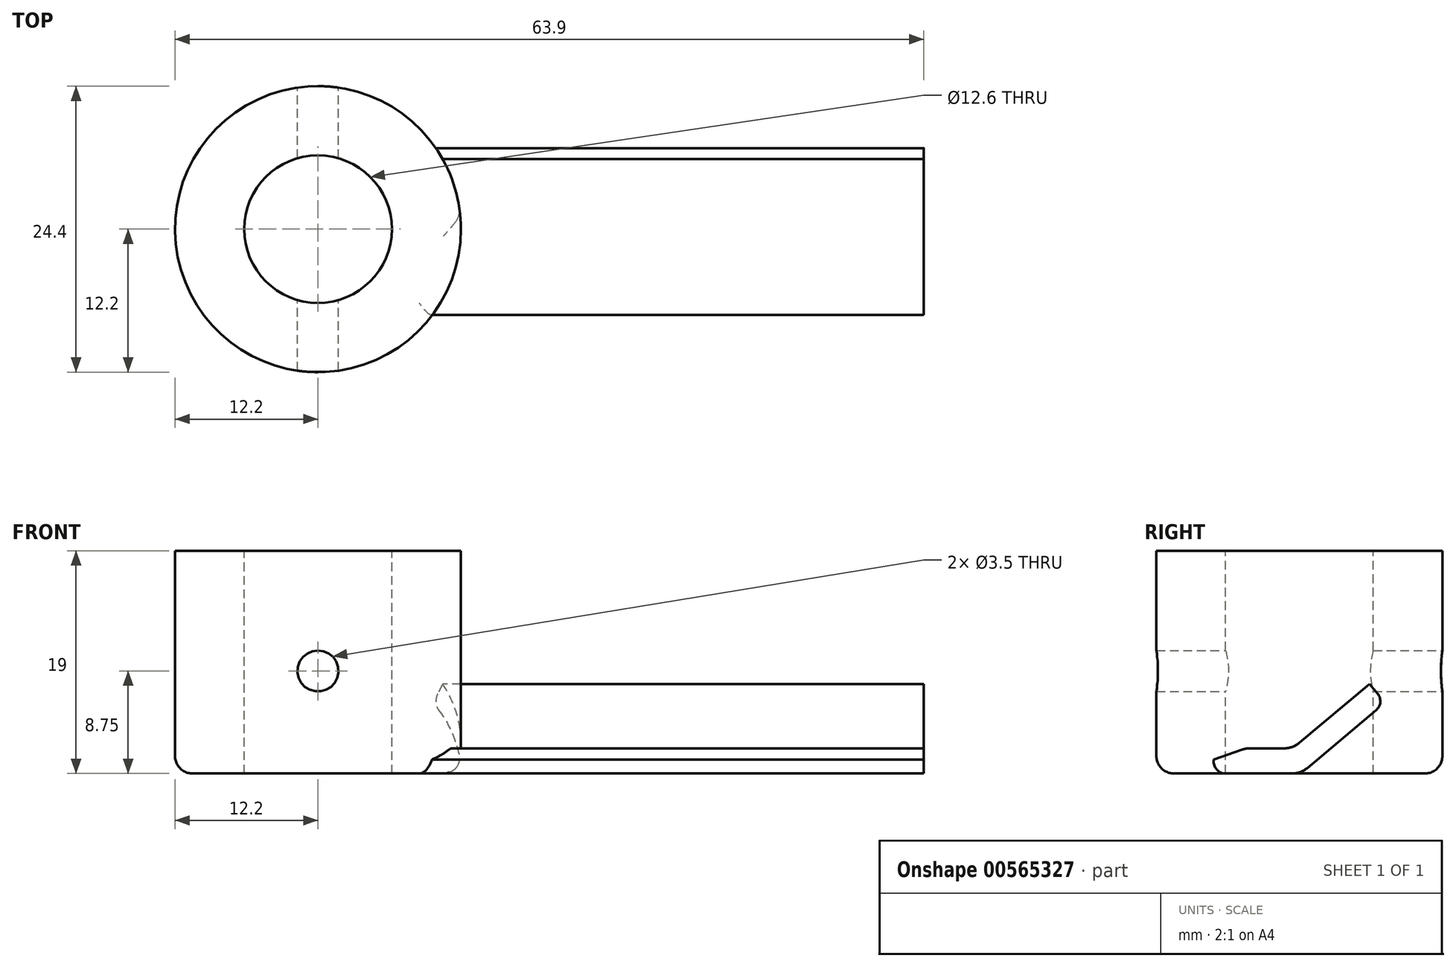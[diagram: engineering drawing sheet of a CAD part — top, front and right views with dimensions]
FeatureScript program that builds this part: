
annotation { "Feature Type Name" : "Feature", "Feature Type Description" : "" }
export const myFeature = defineFeature(function(context is Context, id is Id, definition is map)
    precondition{}
    {
        {
            var Q0;
            Q0=qCreatedBy(makeId("Top.planeOp"),FACE);
            var sketch = newSketch(context, id + "F0", { "sketchPlane" : qUnion([Q0])});
            skCircle(sketch, "E0", {"center": v(0, 0) * mm, "radius": 12.2 * mm});
            skSolve(sketch);
        }
        {
            var Q0;
            Q0 = qSketchRegion(id + "F0", true);
            extrude(context, id + "F1", {"entities" : qUnion([Q0]), "depth" : 19 * mm, "offsetDistance" : 25 * mm});
        }
        {
            var Q0;
            Q0=qCreatedBy(makeId("Right.planeOp"),FACE);
            var sketch = newSketch(context, id + "F2", { "sketchPlane" : qUnion([Q0])});
            skLineSegment(sketch, "E1", {"start": v(-7.31, 0) * mm, "end": v(-7.31, 1.2) * mm});
            skLineSegment(sketch, "E2", {"start": v(-7.31, 1.2) * mm, "end": v(-4.56, 2.15) * mm});
            skLineSegment(sketch, "E3", {"start": v(-4.56, 2.15) * mm, "end": v(-0.56, 2.15) * mm});
            skLineSegment(sketch, "E4", {"start": v(-0.56, 2.15) * mm, "end": v(5.97, 7.64) * mm});
            skLineSegment(sketch, "E5", {"start": v(5.97, 7.64) * mm, "end": v(7.31, 6.05) * mm});
            skLineSegment(sketch, "E6", {"start": v(7.31, 6.05) * mm, "end": v(0.11, 0) * mm});
            skLineSegment(sketch, "E7", {"start": v(0.11, 0) * mm, "end": v(-7.31, 0) * mm});
            skSolve(sketch);
        }
        {
            var Q0;
            Q0 = qSketchRegion(id + "F2", true);
            extrude(context, id + "F3", {"entities" : qUnion([Q0]), "operationType" : NewBodyOperationType.ADD, "depth" : 51.7 * mm, "offsetDistance" : 25 * mm});
        }
        {
            var Q0;
            Q0=makeQuery(id+"F1.opExtrude","CAP_FACE",FACE,{"disambiguationData":[OSD([sQuery(id+"F0.wireOp",EDGE,"E0")])],"isStart":false});
            var sketch = newSketch(context, id + "F4", { "sketchPlane" : qUnion([Q0])});
            skCircle(sketch, "E8", {"center": v(0, 0) * mm, "radius": 6.3 * mm});
            skSolve(sketch);
        }
        {
            var Q0;
            Q0 = qSketchRegion(id + "F4", true);
            extrude(context, id + "F5", {"entities" : qUnion([Q0]), "operationType" : NewBodyOperationType.REMOVE, "oppositeDirection" : true, "depth" : 25 * mm, "offsetDistance" : 25 * mm});
        }
        {
            var Q0;
            Q0=qCreatedBy(makeId("Front.planeOp"),FACE);
            var sketch = newSketch(context, id + "F6", { "sketchPlane" : qUnion([Q0])});
            skCircle(sketch, "E9", {"center": v(0, 8.75) * mm, "radius": 1.75 * mm});
            skPoint(sketch, "E10", {"position": v(-12.2, 19) * mm});
            skSolve(sketch);
        }
        {
            var Q0;
            Q0=makeQuery(id+"F6.imprint","IMPRINT",FACE,{"disambiguationData":[TD([[makeQuery(id+"F6.imprint","IMPRINT",EDGE,{"derivedFrom":sQuery(id+"F6.wireOp",EDGE,"E9")}),1.0]])]});
            var Q1;
            Q1=sQuery(id+"F6.wireOp",EDGE,"E9");
            extrude(context, id + "F7", {"entities" : qUnion([Q0]), "operationType" : NewBodyOperationType.REMOVE, "surfaceEntities" : qUnion([Q1]), "endBound" : BoundingType.THROUGH_ALL, "depth" : 25 * mm, "offsetDistance" : 25 * mm, "hasSecondDirection" : true, "secondDirectionBound" : SecondDirectionBoundingType.THROUGH_ALL, "secondDirectionOppositeDirection" : true, "secondDirectionDepth" : 25 * mm});
        }
        {
            var Q0;
            Q0=makeQuery(id+"F1.opExtrude","CAP_EDGE",EDGE,{"disambiguationData":[OSD([sQuery(id+"F0.wireOp",EDGE,"E0")])],"isStart":true});
            fillet(context, id + "F8", {"entities" : qUnion([Q0]), "radius" : 1.5 * mm, "tangentPropagation" : true, "allowEdgeOverflow" : false});
        }
        {
            var Q0;
            Q0=makeQuery(id+"F3.opExtrude","SWEPT_EDGE",EDGE,{"disambiguationData":[OSD([sQuery(id+"F2.wireOp",EDGE,"E6"),sQuery(id+"F2.wireOp",EDGE,"E7")])]});
            var Q1;
            Q1=makeQuery(id+"F3.opExtrude","SWEPT_EDGE",EDGE,{"disambiguationData":[OSD([sQuery(id+"F2.wireOp",EDGE,"E3"),sQuery(id+"F2.wireOp",EDGE,"E4")])]});
            var Q2;
            Q2=makeQuery(id+"F3.opExtrude","SWEPT_EDGE",EDGE,{"disambiguationData":[OSD([sQuery(id+"F2.wireOp",EDGE,"E2"),sQuery(id+"F2.wireOp",EDGE,"E3")])]});
            fillet(context, id + "F9", {"entities" : qUnion([Q0, Q1, Q2]), "radius" : 2 * mm, "tangentPropagation" : true, "allowEdgeOverflow" : false});
        }
        {
            var Q0;
            Q0=makeQuery(id+"F3.opExtrude","SWEPT_EDGE",EDGE,{"disambiguationData":[OSD([sQuery(id+"F2.wireOp",EDGE,"E5"),sQuery(id+"F2.wireOp",EDGE,"E6")])]});
            var Q1;
            Q1=makeQuery(id+"F3.opExtrude","SWEPT_EDGE",EDGE,{"disambiguationData":[OSD([sQuery(id+"F2.wireOp",EDGE,"E1"),sQuery(id+"F2.wireOp",EDGE,"E7")])]});
            fillet(context, id + "F10", {"entities" : qUnion([Q0, Q1]), "radius" : 1 * mm, "tangentPropagation" : true, "allowEdgeOverflow" : false});
        }
    });
